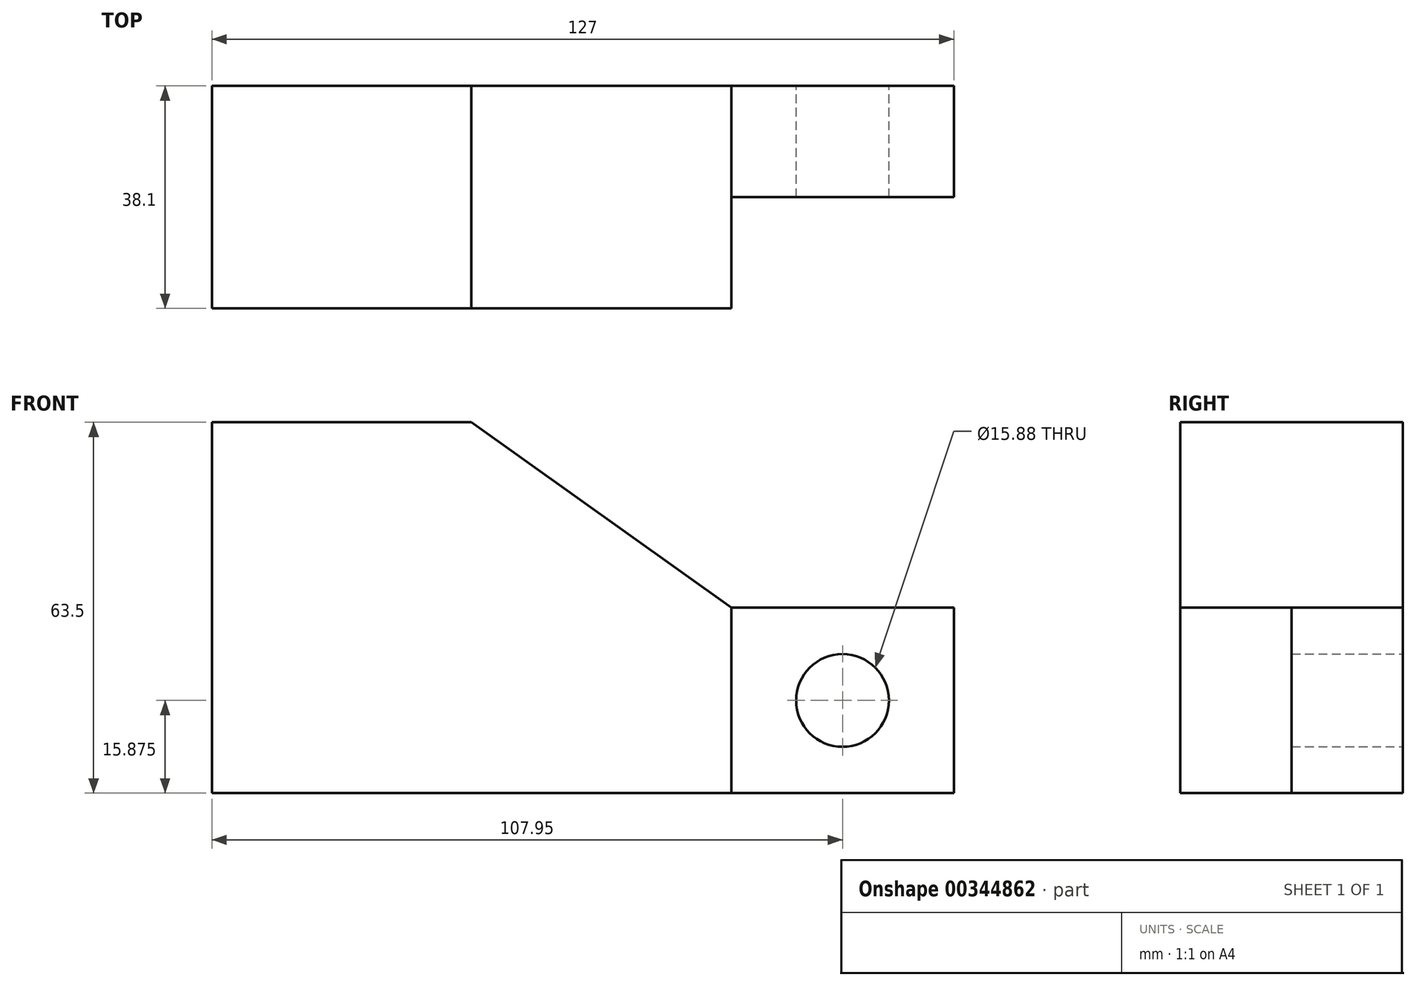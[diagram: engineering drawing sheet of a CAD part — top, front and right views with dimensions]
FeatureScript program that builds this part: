
annotation { "Feature Type Name" : "Feature", "Feature Type Description" : "" }
export const myFeature = defineFeature(function(context is Context, id is Id, definition is map)
    precondition{}
    {
        {
            var Q0;
            Q0=qCreatedBy(makeId("Front.planeOp"),FACE);
            var sketch = newSketch(context, id + "F0", { "sketchPlane" : qUnion([Q0])});
            skLineSegment(sketch, "E0.bottom", {"start": v(0, 31.75) * mm, "end": v(-44.45, 31.75) * mm});
            skLineSegment(sketch, "E0.top", {"start": v(44.45, -31.75) * mm, "end": v(-44.45, -31.75) * mm});
            skLineSegment(sketch, "E0.right", {"start": v(-44.45, 31.75) * mm, "end": v(-44.45, -31.75) * mm});
            skPoint(sketch, "E0.middle", {"position": v(0, 0) * mm});
            skLineSegment(sketch, "E1", {"start": v(44.45, 0) * mm, "end": v(0, 31.75) * mm});
            skPoint(sketch, "E2.orphan", {"position": v(44.45, 31.75) * mm});
            skLineSegment(sketch, "E3", {"start": v(44.45, 0) * mm, "end": v(44.45, -31.75) * mm});
            skLineSegment(sketch, "E4.bottom", {"start": v(44.45, 0) * mm, "end": v(82.55, 0) * mm});
            skLineSegment(sketch, "E4.top", {"start": v(44.45, -31.75) * mm, "end": v(82.55, -31.75) * mm});
            skLineSegment(sketch, "E4.right", {"start": v(82.55, 0) * mm, "end": v(82.55, -31.75) * mm});
            skCircle(sketch, "E5", {"center": v(63.5, -15.88) * mm, "radius": 7.94 * mm});
            skSolve(sketch);
        }
        {
            var Q0;
            Q0=makeQuery(id+"F0.imprint","IMPRINT",FACE,{"disambiguationData":[TD([[makeQuery(id+"F0.imprint","IMPRINT",EDGE,{"derivedFrom":sQuery(id+"F0.wireOp",EDGE,"E0.bottom")}),1.0]])]});
            extrude(context, id + "F1", {"entities" : qUnion([Q0]), "depth" : 38.1 * mm});
        }
        {
            var Q0;
            Q0=makeQuery(id+"F0.imprint","IMPRINT",FACE,{"disambiguationData":[TD([[makeQuery(id+"F0.imprint","IMPRINT",EDGE,{"derivedFrom":sQuery(id+"F0.wireOp",EDGE,"E4.bottom")}),-1.0]])]});
            extrude(context, id + "F2", {"entities" : qUnion([Q0]), "operationType" : NewBodyOperationType.ADD, "depth" : 19.05 * mm});
        }
    });
